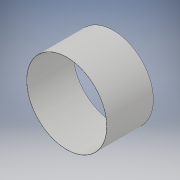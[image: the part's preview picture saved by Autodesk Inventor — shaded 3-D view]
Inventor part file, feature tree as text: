
AUTODESK INVENTOR PART (.ipt)
format: ipt  version: 2019 (Build 230136000, 136)  size: 102,912 bytes
history: native  units: mm
features: extrude x2, sketch x2
ambient origin geometry x8: Origin, YZ Plane, XZ Plane, XY Plane, X Axis, Y Axis, Z Axis, Center Point
bodies: Solid1 (feature_tree)
feature tree (4):
  extrude  "Extrusion1"  Depth=11.68mm TaperAngle=0.0deg
  extrude  "Extrusion2"  Depth=11.68mm TaperAngle=0.0deg
  sketch  "Sketch1"  dims[d0=20.17mm d1=11.68mm d2=0.0mm]
  sketch  "Sketch2"  dims[d3=20.07mm d4=11.68mm d5=0.0mm]
